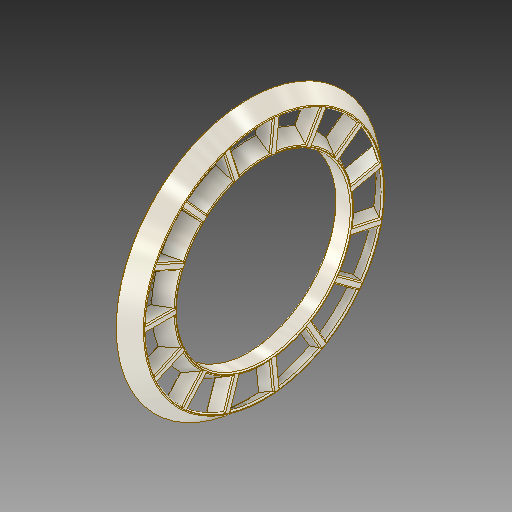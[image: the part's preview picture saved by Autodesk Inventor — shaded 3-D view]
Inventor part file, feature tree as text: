
AUTODESK INVENTOR PART (.ipt)
format: ipt  version: 2019 (Build 230136000, 136)  size: 856,576 bytes
history: native  units: mm
features: sketch x2, revolve x2, split x2, other x2, extrude x1, plane x1, pattern_circular x1, boolean_combine x1, surface_op x1
ambient origin geometry x8: Origin, YZ Plane, XZ Plane, XY Plane, X Axis, Y Axis, Z Axis, Center Point
bodies: Solid3 (feature_tree), Solid2 (feature_tree)
feature tree (13):
  sketch  "Sketch1"  dims[d11=90.0deg d12=90.0deg]
  revolve  "Revolution1"  Angle=90.0deg
  revolve  "Revolution2"  [1 undecoded]
  extrude  "Extrusion1"  TaperAngle=0.0deg  [1 undecoded]
  plane  "Work Plane1"
  split  "Split1"
  split  "Split2"
  pattern_circular  "Circular Pattern1"  Count=15 Angle=360.0deg
  boolean_combine  "Combine1"
  other  "Rule Fillet1"
  sketch  "Sketch2"  dims[d13=6.0mm d14=10.0mm d15=0.0mm d16=0.0mm d17=150.0mm d18=360.0deg d20=1.0mm d22=10.5mm d23=15.0mm d24=2.0mm d25=5.0mm d26=77.75mm d27=26.0mm d28=1.0mm d29=4.0mm d31=9.5mm]
  surface_op  "Surface1"
  other  "Srf2"
note: 2 required parameter values undecoded (feature->parameter linkage not recoverable at this tier; creation-order binding heuristic only, values carry confidence <= 0.55)